SOLIDWORKS PART (.sldprt)
format: sldprt  version: not decoded by parser v0  size: 122,880 bytes
history: native  units: mm
features: sketch x10, plane x5, extrude x4, material x1, sweep x1 (+13 scaffold rows collapsed)
feature tree (34):
  scaffold x13  (default folders/planes/origin — collapsed)
  material  "材质 <未指定>"
  plane  "前视基准面"
  plane  "上视基准面"
  plane  "右视基准面"
  sketch  "草图1"  dims[D4=10.0mm D1=135.0mm D2=50.0mm D3=30.0mm]
  sketch  "草图2"  dims[D1=5.0mm]
  sweep  "扫描1"
  sketch  "草图4"  dims[D1=85.0mm]
  sketch  "草图12"  dims[D1=15.0mm]
  sketch  "草图13"  dims[D1=10.0mm]
  extrude  "凸台-拉伸7"  Depth=30mm
  sketch  "草图11"
  sketch  "草图14"  dims[D1=75.0mm]
  extrude  "凸台-拉伸8"  Depth=30mm
  plane  "基准面1"
  sketch  "草图15"  dims[D1=15.0mm]
  extrude  "凸台-拉伸9"  Depth=75mm
  sketch  "草图16"  dims[D1=15.0mm]
  plane  "基准面2"
  sketch  "草图17"  dims[D1=~1.837415mm]
  extrude  "凸台-拉伸10"  Depth=10mm
decode coverage: 13 of 15 modeling features carry decoded parameters
note: ~ marks probable driven/reference dimensions
note: suppression state not decoded; provenance and decode notes live in map.json
